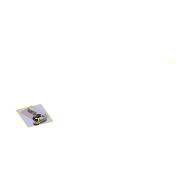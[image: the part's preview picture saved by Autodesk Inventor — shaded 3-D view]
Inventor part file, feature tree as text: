
AUTODESK INVENTOR PART (.ipt)
format: ipt  version: 2016 (Build 200138000, 138)  size: 853,504 bytes
history: native  units: in
note: dims shown in document units (in); Inventor stores cm internally (conversion verified against a paired STEP export)
features: extrude x4, sketch x4, plane x2, fillet x2, other x1, mirror x1, imported_body x1, projected_geometry x1
ambient origin geometry x8: Origin, YZ Plane, XZ Plane, XY Plane, X Axis, Y Axis, Z Axis, Center Point
bodies: Solid1 (feature_tree), Solid2 (feature_tree)
feature tree (16):
  other  "033-fe_lever-0425_stp.ipt1"
  plane  "Work Plane1"
  extrude  "Extrusion1"  Depth=0.0512in
  fillet  "Fillet1"  Radius=0.1378in
  plane  "Work Plane2"
  mirror  "Mirror1"
  extrude  "Extrusion2"  Depth=0.0787in TaperAngle=0.0deg
  fillet  "Fillet2"  Radius=0.0787in
  extrude  "Extrusion4"  Depth=0.1969in
  extrude  "Extrusion5"  [1 undecoded]
  imported_body  "Base1"
  sketch  "Sketch1"  dims[d0=-0.0787in d1=0.0512in d2=0.1378in d3=0.0in]
  sketch  "Sketch3"  dims[d4=0.0244in d5=0.0787in d6=0.0in d7=0.0787in]
  sketch  "Sketch8"  dims[d9=0.0315in d14=0.1969in d15=-0.0069in]
  sketch  "Sketch9"  dims[d17=0.1969in d18=-0.0069in]
  projected_geometry  "Project Cut Edges1"
note: 1 required parameter value undecoded (feature->parameter linkage not recoverable at this tier; creation-order binding heuristic only, values carry confidence <= 0.55)
